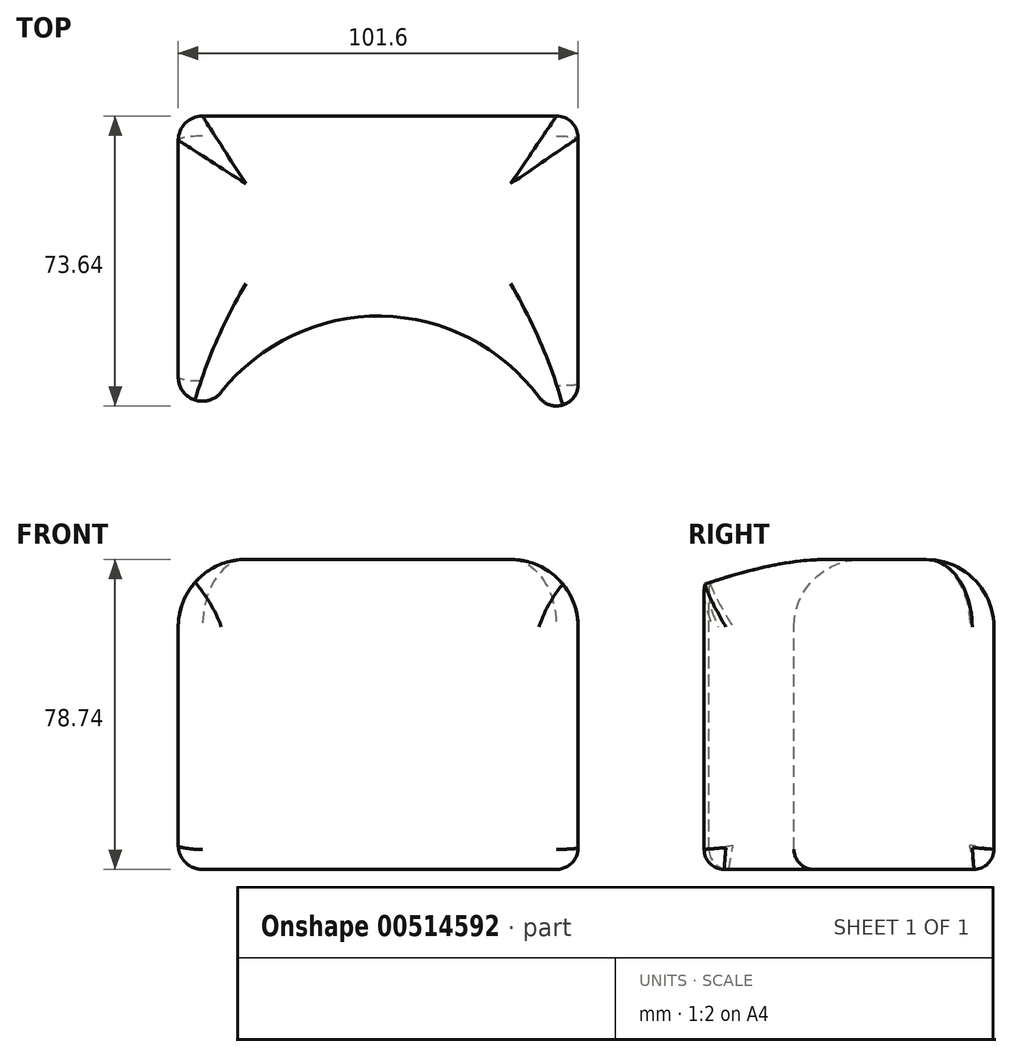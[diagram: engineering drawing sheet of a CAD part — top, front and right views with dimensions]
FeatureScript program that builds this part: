
annotation { "Feature Type Name" : "Feature", "Feature Type Description" : "" }
export const myFeature = defineFeature(function(context is Context, id is Id, definition is map)
    precondition{}
    {
        {
            var Q0;
            Q0=qCreatedBy(makeId("Top.planeOp"),FACE);
            var sketch = newSketch(context, id + "F0", { "sketchPlane" : qUnion([Q0])});
            skLineSegment(sketch, "E0.bottom", {"start": v(-49.69, 36.24) * mm, "end": v(51.91, 36.24) * mm});
            skLineSegment(sketch, "E0.top", {"start": v(-49.69, -65.36) * mm, "end": v(51.91, -65.36) * mm});
            skLineSegment(sketch, "E0.left", {"start": v(-49.69, 36.24) * mm, "end": v(-49.69, -65.36) * mm});
            skLineSegment(sketch, "E0.right", {"start": v(51.91, 36.24) * mm, "end": v(51.91, -65.36) * mm});
            skSolve(sketch);
        }
        {
            var Q0;
            Q0=makeQuery(id+"F0.imprint","IMPRINT",FACE,{"disambiguationData":[TD([[makeQuery(id+"F0.imprint","IMPRINT",EDGE,{"derivedFrom":sQuery(id+"F0.wireOp",EDGE,"E0.bottom")}),-1.0]])]});
            extrude(context, id + "F1", {"entities" : qUnion([Q0]), "depth" : 53.34 * mm, "offsetDistance" : 25.4 * mm});
        }
        {
            var Q0;
            Q0=makeQuery(id+"F1.opExtrude","CAP_FACE",FACE,{"disambiguationData":[OSD([sQuery(id+"F0.wireOp",EDGE,"E0.bottom"),sQuery(id+"F0.wireOp",EDGE,"E0.top"),sQuery(id+"F0.wireOp",EDGE,"E0.left"),sQuery(id+"F0.wireOp",EDGE,"E0.right")])],"isStart":false});
            var sketch = newSketch(context, id + "F2", { "sketchPlane" : qUnion([Q0])});
            skArc(sketch, "E1", {"start": v(51.91, -65.36) * mm, "mid": v(1.11, -14.56) * mm, "end": v(-49.69, -65.36) * mm});
            skSolve(sketch);
        }
        {
            var Q0;
            Q0=makeQuery(id+"F2.imprint","IMPRINT",FACE,{"disambiguationData":[TD([[makeQuery(id+"F2.imprint","IMPRINT",EDGE,{"derivedFrom":sQuery(id+"F2.wireOp",EDGE,"E1")}),1.0]])]});
            extrude(context, id + "F3", {"entities" : qUnion([Q0]), "operationType" : NewBodyOperationType.REMOVE, "oppositeDirection" : true, "depth" : 62.23 * mm, "offsetDistance" : 25.4 * mm});
        }
        {
            var Q0;
            Q0=makeQuery(id+"F1.opExtrude","CAP_FACE",FACE,{"disambiguationData":[OSD([sQuery(id+"F0.wireOp",EDGE,"E0.bottom"),sQuery(id+"F0.wireOp",EDGE,"E0.top"),sQuery(id+"F0.wireOp",EDGE,"E0.left"),sQuery(id+"F0.wireOp",EDGE,"E0.right")])],"isStart":false});
            var sketch = newSketch(context, id + "F4", { "sketchPlane" : qUnion([Q0])});
            skLineSegment(sketch, "E2.bottom", {"start": v(-49.69, -65.36) * mm, "end": v(51.91, -65.36) * mm});
            skLineSegment(sketch, "E2.top", {"start": v(-49.69, -50.05) * mm, "end": v(51.91, -50.05) * mm});
            skLineSegment(sketch, "E2.left", {"start": v(-49.69, -65.36) * mm, "end": v(-49.69, -50.05) * mm});
            skLineSegment(sketch, "E2.right", {"start": v(51.91, -65.36) * mm, "end": v(51.91, -50.05) * mm});
            skSolve(sketch);
        }
        {
            var Q0;
            {var subQ0=sQuery(id+"F4.wireOp",EDGE,"E2.bottom");Q0=makeQuery(id+"F4.imprint","IMPRINT",FACE,{"disambiguationData":[TD([[makeQuery(id+"F4.imprint","IMPRINT",EDGE,{"derivedFrom":subQ0}),1.0]])]});}
            extrude(context, id + "F5", {"entities" : qUnion([Q0]), "operationType" : NewBodyOperationType.REMOVE, "oppositeDirection" : true, "depth" : 61.47 * mm, "offsetDistance" : 25.4 * mm});
        }
        {
            var Q0;
            Q0=makeQuery(id+"F1.opExtrude","CAP_FACE",FACE,{"disambiguationData":[OSD([sQuery(id+"F0.wireOp",EDGE,"E0.bottom"),sQuery(id+"F0.wireOp",EDGE,"E0.top"),sQuery(id+"F0.wireOp",EDGE,"E0.left"),sQuery(id+"F0.wireOp",EDGE,"E0.right")])],"isStart":false});
            extrude(context, id + "F6", {"entities" : qUnion([Q0]), "operationType" : NewBodyOperationType.ADD, "depth" : 25.4 * mm, "offsetDistance" : 25.4 * mm});
        }
        {
            var Q0;
            Q0=makeQuery(id+"F6.opExtrude","CAP_FACE",FACE,{"disambiguationData":[OSD([sQuery(id+"F0.wireOp",EDGE,"E0.bottom"),sQuery(id+"F0.wireOp",EDGE,"E0.top"),sQuery(id+"F0.wireOp",EDGE,"E0.left"),sQuery(id+"F0.wireOp",EDGE,"E0.right")])],"isStart":false});
            fillet(context, id + "F7", {"entities" : qUnion([Q0]), "radius" : 17.17 * mm, "tangentPropagation" : true, "allowEdgeOverflow" : false});
        }
        {
            var Q0;
            {var subQ0=sQuery(id+"F0.wireOp",EDGE,"E0.right");Q0=makeQuery(id+"F6.boolean.opBoolean","MERGE",FACE,{"derivedFrom":[makeQuery(id+"F1.opExtrude","SWEPT_FACE",FACE,{"disambiguationData":[OSD([subQ0])]}),makeQuery(id+"F6.opExtrude","SWEPT_FACE",FACE,{"disambiguationData":[OSD([subQ0])]})]});}
            fillet(context, id + "F8", {"entities" : qUnion([Q0]), "radius" : 5.52 * mm, "tangentPropagation" : true, "allowEdgeOverflow" : false});
        }
        {
            var Q0;
            {var subQ0=sQuery(id+"F0.wireOp",EDGE,"E0.left");Q0=makeQuery(id+"F6.boolean.opBoolean","MERGE",FACE,{"derivedFrom":[makeQuery(id+"F1.opExtrude","SWEPT_FACE",FACE,{"disambiguationData":[OSD([subQ0])]}),makeQuery(id+"F6.opExtrude","SWEPT_FACE",FACE,{"disambiguationData":[OSD([subQ0])]})]});}
            fillet(context, id + "F9", {"entities" : qUnion([Q0]), "radius" : 6.13 * mm, "tangentPropagation" : true, "allowEdgeOverflow" : false});
        }
        {
            var Q0;
            Q0=makeQuery(id+"F1.opExtrude","CAP_FACE",FACE,{"disambiguationData":[OSD([sQuery(id+"F0.wireOp",EDGE,"E0.bottom"),sQuery(id+"F0.wireOp",EDGE,"E0.top"),sQuery(id+"F0.wireOp",EDGE,"E0.left"),sQuery(id+"F0.wireOp",EDGE,"E0.right")])],"isStart":true});
            fillet(context, id + "F10", {"entities" : qUnion([Q0]), "radius" : 5.08 * mm, "tangentPropagation" : true, "allowEdgeOverflow" : false});
        }
    });
